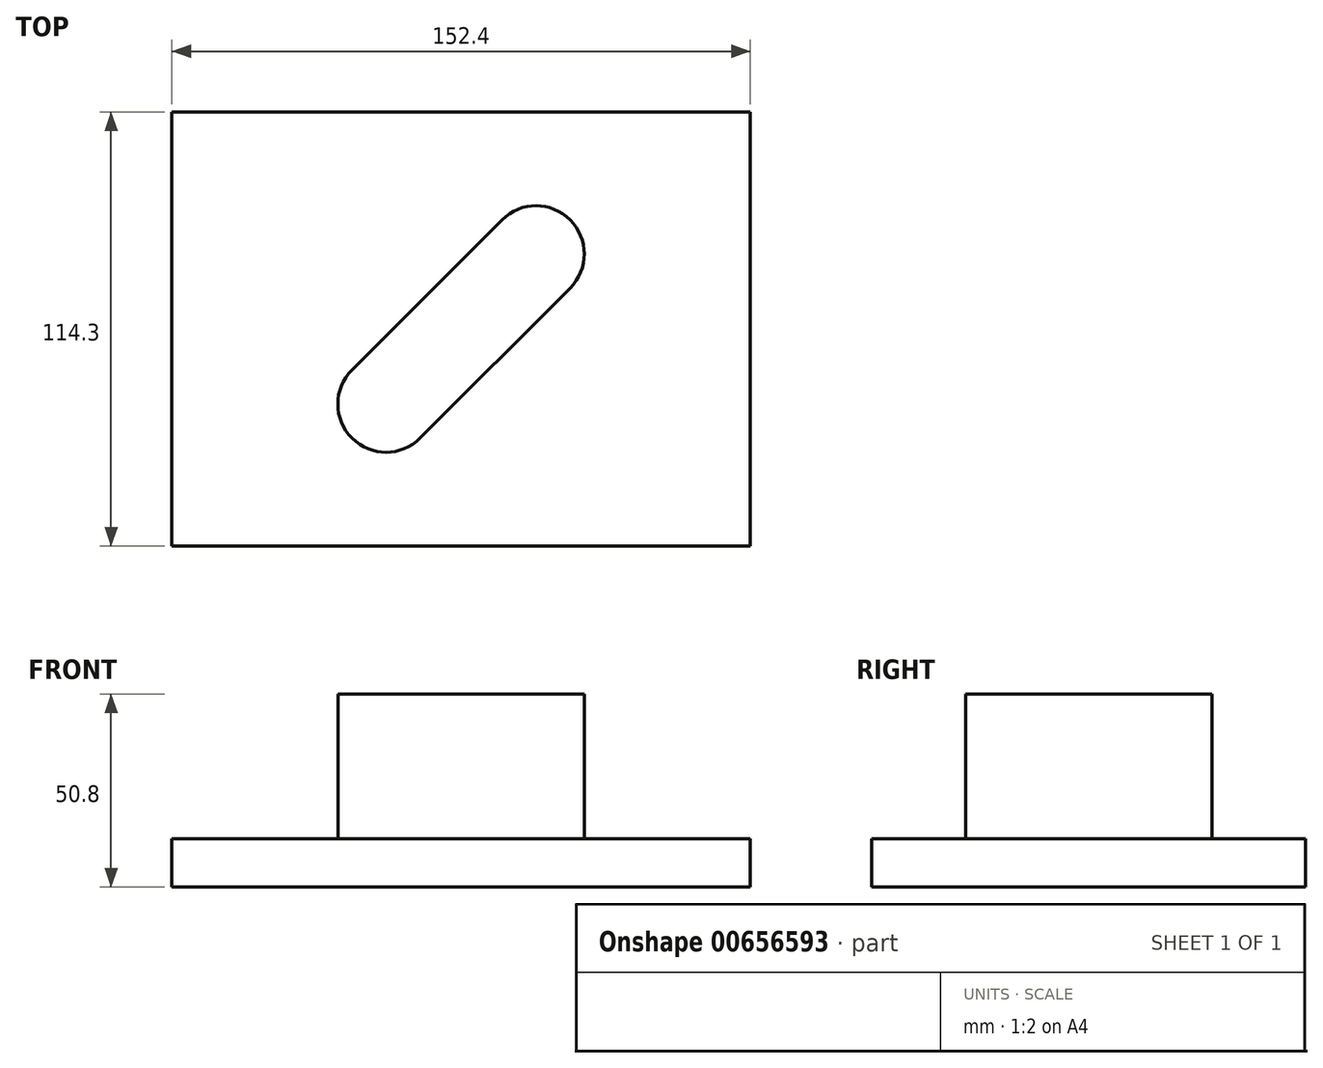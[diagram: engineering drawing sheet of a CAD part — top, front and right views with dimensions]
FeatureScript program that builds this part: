
annotation { "Feature Type Name" : "Feature", "Feature Type Description" : "" }
export const myFeature = defineFeature(function(context is Context, id is Id, definition is map)
    precondition{}
    {
        {
            var Q0;
            Q0=qCreatedBy(makeId("Top.planeOp"),FACE);
            var sketch = newSketch(context, id + "F0", { "sketchPlane" : qUnion([Q0])});
            skLineSegment(sketch, "E0.bottom", {"start": v(-76.2, 57.15) * mm, "end": v(76.2, 57.15) * mm});
            skLineSegment(sketch, "E0.top", {"start": v(-76.2, -57.15) * mm, "end": v(76.2, -57.15) * mm});
            skLineSegment(sketch, "E0.left", {"start": v(-76.2, 57.15) * mm, "end": v(-76.2, -57.15) * mm});
            skLineSegment(sketch, "E0.right", {"start": v(76.2, 57.15) * mm, "end": v(76.2, -57.15) * mm});
            skPoint(sketch, "E0.middle", {"position": v(0, 0) * mm});
            skSolve(sketch);
        }
        {
            var Q0;
            Q0=makeQuery(id+"F0.imprint","IMPRINT",FACE,{"disambiguationData":[TD([[makeQuery(id+"F0.imprint","IMPRINT",EDGE,{"derivedFrom":sQuery(id+"F0.wireOp",EDGE,"E0.bottom")}),-1.0]])]});
            extrude(context, id + "F1", {"entities" : qUnion([Q0]), "oppositeDirection" : true, "depth" : 12.7 * mm, "offsetDistance" : 25.4 * mm});
        }
        {
            var Q0;
            Q0=makeQuery(id+"F1.opExtrude","CAP_FACE",FACE,{"disambiguationData":[OSD([sQuery(id+"F0.wireOp",EDGE,"E0.bottom"),sQuery(id+"F0.wireOp",EDGE,"E0.top"),sQuery(id+"F0.wireOp",EDGE,"E0.left"),sQuery(id+"F0.wireOp",EDGE,"E0.right")])],"isStart":true});
            var sketch = newSketch(context, id + "F2", { "sketchPlane" : qUnion([Q0])});
            skLineSegment(sketch, "E1", {"start": v(0, 0) * mm, "end": v(-28.74, -28.74) * mm});
            skLineSegment(sketch, "E2", {"start": v(0, 0) * mm, "end": v(28.74, 28.74) * mm});
            skLineSegment(sketch, "E3", {"start": v(-28.74, -28.74) * mm, "end": v(-37.72, -19.76) * mm});
            skLineSegment(sketch, "E4", {"start": v(-28.74, -28.74) * mm, "end": v(-19.76, -37.72) * mm});
            skLineSegment(sketch, "E5", {"start": v(28.74, 28.74) * mm, "end": v(19.76, 37.72) * mm});
            skLineSegment(sketch, "E6", {"start": v(28.74, 28.74) * mm, "end": v(37.72, 19.76) * mm});
            skLineSegment(sketch, "E7", {"start": v(-37.72, -19.76) * mm, "end": v(19.76, 37.72) * mm});
            skLineSegment(sketch, "E8", {"start": v(-19.76, -37.72) * mm, "end": v(37.72, 19.76) * mm});
            skLineSegment(sketch, "E9", {"start": v(-28.74, -10.78) * mm, "end": v(-10.78, -28.74) * mm});
            skLineSegment(sketch, "E10", {"start": v(10.78, 28.74) * mm, "end": v(28.74, 10.78) * mm});
            skArc(sketch, "E11", {"start": v(-28.74, -10.78) * mm, "mid": v(-28.74, -28.74) * mm, "end": v(-10.78, -28.74) * mm});
            skArc(sketch, "E12", {"start": v(28.74, 10.78) * mm, "mid": v(28.74, 28.74) * mm, "end": v(10.78, 28.74) * mm});
            skSolve(sketch);
        }
        {
            var Q0;
            {var subQ1=sQuery(id+"F2.wireOp",EDGE,"E1");var subQ3=sQuery(id+"F2.wireOp",EDGE,"E9");var subQ4=makeQuery(id+"F2.imprint","INTERSECT",VERTEX,{"derivedFrom":[subQ1,subQ3]});Q0=makeQuery(id+"F2.imprint","IMPRINT",FACE,{"disambiguationData":[TD([[makeQuery(id+"F2.imprint","IMPRINT",EDGE,{"disambiguationData":[TD([[subQ4,1.0]])],"derivedFrom":subQ3}),-1.0]])]});}
            var Q1;
            {var subQ1=sQuery(id+"F2.wireOp",EDGE,"E1");var subQ3=sQuery(id+"F2.wireOp",EDGE,"E9");var subQ4=makeQuery(id+"F2.imprint","INTERSECT",VERTEX,{"derivedFrom":[subQ1,subQ3]});Q1=makeQuery(id+"F2.imprint","IMPRINT",FACE,{"disambiguationData":[TD([[makeQuery(id+"F2.imprint","IMPRINT",EDGE,{"disambiguationData":[TD([[subQ4,-1.0]])],"derivedFrom":subQ3}),-1.0]])]});}
            var Q2;
            {var subQ1=sQuery(id+"F2.wireOp",EDGE,"E2");var subQ3=sQuery(id+"F2.wireOp",EDGE,"E10");var subQ4=makeQuery(id+"F2.imprint","INTERSECT",VERTEX,{"derivedFrom":[subQ1,subQ3]});Q2=makeQuery(id+"F2.imprint","IMPRINT",FACE,{"disambiguationData":[TD([[makeQuery(id+"F2.imprint","IMPRINT",EDGE,{"disambiguationData":[TD([[subQ4,1.0]])],"derivedFrom":subQ3}),1.0]])]});}
            var Q3;
            {var subQ1=sQuery(id+"F2.wireOp",EDGE,"E2");var subQ3=sQuery(id+"F2.wireOp",EDGE,"E10");var subQ4=makeQuery(id+"F2.imprint","INTERSECT",VERTEX,{"derivedFrom":[subQ1,subQ3]});Q3=makeQuery(id+"F2.imprint","IMPRINT",FACE,{"disambiguationData":[TD([[makeQuery(id+"F2.imprint","IMPRINT",EDGE,{"disambiguationData":[TD([[subQ4,-1.0]])],"derivedFrom":subQ3}),1.0]])]});}
            var Q4;
            {var subQ5=sQuery(id+"F2.wireOp",EDGE,"E2");var subQ6=sQuery(id+"F2.wireOp",EDGE,"E1");var subQ7=makeQuery(id+"F2.imprint","INTERSECT",VERTEX,{"derivedFrom":[subQ6,subQ5]});Q4=makeQuery(id+"F2.imprint","IMPRINT",FACE,{"disambiguationData":[TD([[makeQuery(id+"F2.imprint","IMPRINT",EDGE,{"disambiguationData":[TD([[subQ7,-1.0]])],"derivedFrom":subQ6}),1.0]])]});}
            var Q5;
            {var subQ3=sQuery(id+"F2.wireOp",EDGE,"E1");var subQ7=sQuery(id+"F2.wireOp",EDGE,"E2");var subQ8=makeQuery(id+"F2.imprint","INTERSECT",VERTEX,{"derivedFrom":[subQ3,subQ7]});Q5=makeQuery(id+"F2.imprint","IMPRINT",FACE,{"disambiguationData":[TD([[makeQuery(id+"F2.imprint","IMPRINT",EDGE,{"disambiguationData":[TD([[subQ8,-1.0]])],"derivedFrom":subQ3}),-1.0]])]});}
            extrude(context, id + "F3", {"entities" : qUnion([Q0, Q1, Q2, Q3, Q4, Q5]), "operationType" : NewBodyOperationType.ADD, "depth" : 38.1 * mm, "offsetDistance" : 25.4 * mm});
        }
    });
